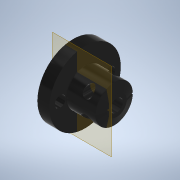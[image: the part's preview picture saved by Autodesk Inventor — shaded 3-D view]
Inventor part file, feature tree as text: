
AUTODESK INVENTOR PART (.ipt)
format: ipt  version: 2022 (Build 260153000, 153)  size: 231,424 bytes
history: native  units: in
note: dims shown in document units (in); Inventor stores cm internally (conversion verified against a paired STEP export)
features: sketch x5, extrude x4, revolve x1, fillet x1, plane x1, pattern_circular x1
ambient origin geometry x8: Origin, YZ Plane, XZ Plane, XY Plane, X Axis, Y Axis, Z Axis, Center Point
bodies: Solid1 (feature_tree)
feature tree (13):
  revolve  "Revolution1"  [1 undecoded]
  fillet  "Fillet1"  Radius=0.125in
  extrude  "Extrusion1"  Depth=0.45in
  extrude  "Extrusion2"  Depth=0.2358in
  plane  "Work Plane1"
  extrude  "Extrusion3"  Depth=0.0787in
  pattern_circular  "Circular Pattern1"  [2 undecoded]
  extrude  "Extrusion4"  Depth=0.3685in
  sketch  "Sketch1"  dims[d0=0.675in d1=0.125in d2=0.125in]
  sketch  "Sketch2"  dims[d3=0.15in d4=0.45in]
  sketch  "Sketch3"  dims[d5=0.4in d6=0.2358in]
  sketch  "Sketch4"  dims[d7=0.25in d8=0.0787in]
  sketch  "Sketch5"  dims[d9=360.0deg d10=0.125in d11=0.3685in d12=0.0063in d13=0.225in d14=0.15in d15=0.1181in d16=0.0in d17=0.0in d18=0.5in d19=0.025in d20=0.0in d21=0.1in d22=0.1575in d23=0.225in d25=0.15in d26=0.0in d27=0.0in d28=0.7874in d29=360.0deg d31=0.625in d32=0.138in d33=0.138in d34=0.0in d35=0.0in]
note: 3 required parameter values undecoded (feature->parameter linkage not recoverable at this tier; creation-order binding heuristic only, values carry confidence <= 0.55)